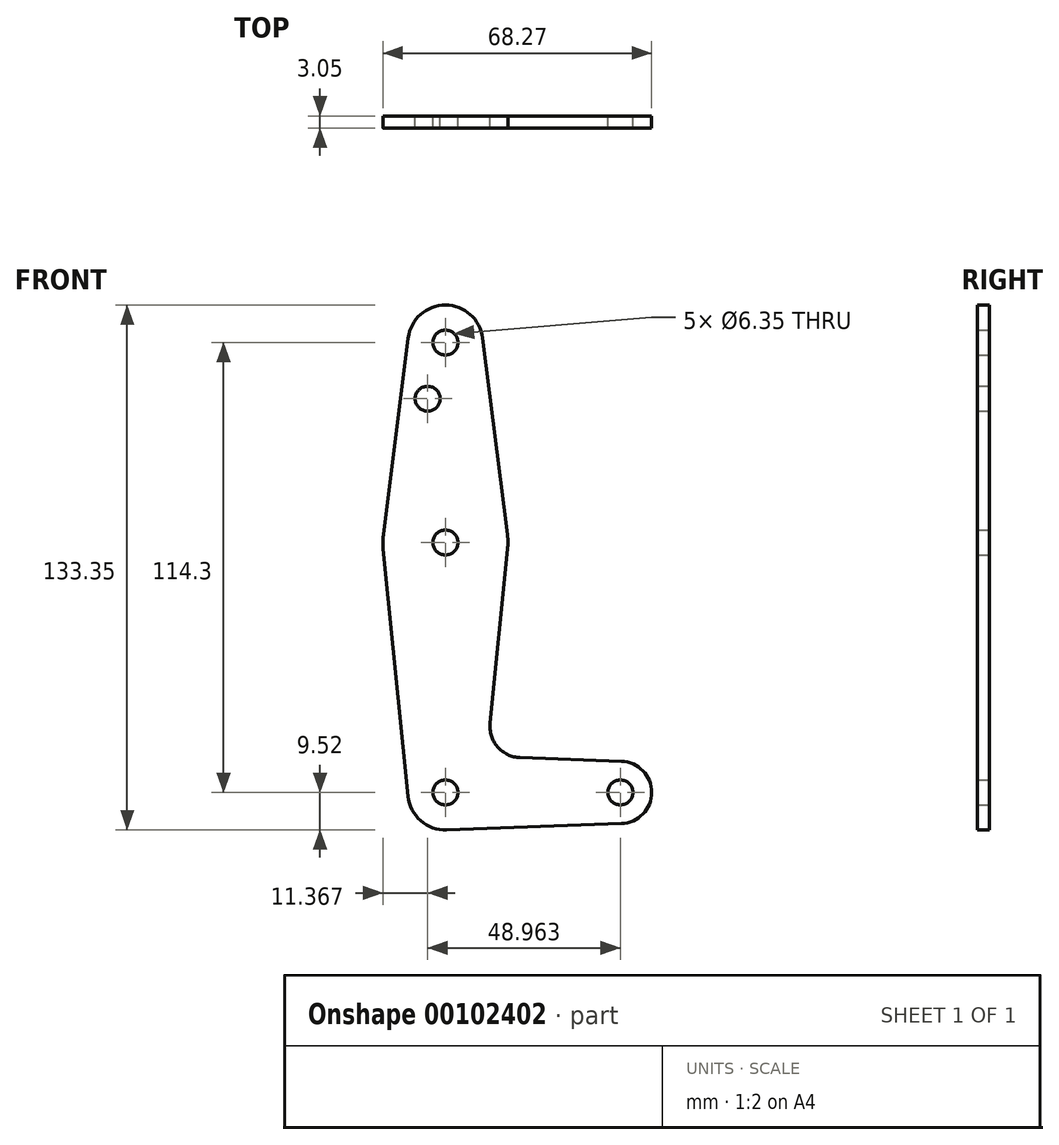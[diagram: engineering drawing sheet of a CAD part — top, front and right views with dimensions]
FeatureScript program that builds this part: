
annotation { "Feature Type Name" : "Feature", "Feature Type Description" : "" }
export const myFeature = defineFeature(function(context is Context, id is Id, definition is map)
    precondition{}
    {
        {
            var Q0;
            Q0=qCreatedBy(makeId("Front.planeOp"),FACE);
            var sketch = newSketch(context, id + "F0", { "sketchPlane" : qUnion([Q0])});
            skLineSegment(sketch, "E0", {"start": v(0, 114.3) * mm, "end": v(0, 0) * mm, "construction": true});
            skLineSegment(sketch, "E1", {"start": v(0, 0) * mm, "end": v(51.84, 0) * mm, "construction": true});
            skCircle(sketch, "E2", {"center": v(0, 114.3) * mm, "radius": 9.53 * mm});
            skCircle(sketch, "E3", {"center": v(0, 63.5) * mm, "radius": 15.88 * mm});
            skCircle(sketch, "E4", {"center": v(0, 0) * mm, "radius": 9.53 * mm});
            skCircle(sketch, "E5", {"center": v(44.45, 0) * mm, "radius": 7.94 * mm});
            skLineSegment(sketch, "E6", {"start": v(-9.45, 115.5) * mm, "end": v(-15.75, 65.48) * mm});
            skLineSegment(sketch, "E7", {"start": v(9.45, 115.5) * mm, "end": v(15.75, 65.48) * mm});
            skLineSegment(sketch, "E8", {"start": v(15.8, 61.91) * mm, "end": v(11.34, 17.6) * mm});
            skLineSegment(sketch, "E9", {"start": v(-15.8, 61.91) * mm, "end": v(-9.48, -0.95) * mm});
            skLineSegment(sketch, "E10", {"start": v(18.97, 8.85) * mm, "end": v(44.73, 7.93) * mm});
            skLineSegment(sketch, "E11", {"start": v(0.34, -9.52) * mm, "end": v(44.73, -7.93) * mm});
            skCircle(sketch, "E12", {"center": v(0, 114.3) * mm, "radius": 3.18 * mm});
            skCircle(sketch, "E13", {"center": v(-4.51, 100.03) * mm, "radius": 3.18 * mm});
            skCircle(sketch, "E14", {"center": v(0, 63.5) * mm, "radius": 3.18 * mm});
            skCircle(sketch, "E15", {"center": v(0, 0) * mm, "radius": 3.18 * mm});
            skCircle(sketch, "E16", {"center": v(44.45, 0) * mm, "radius": 3.18 * mm});
            skArc(sketch, "E17.filletArc", {"start": v(11.34, 17.6) * mm, "mid": v(13.26, 11.57) * mm, "end": v(18.97, 8.85) * mm});
            skSolve(sketch);
        }
        {
            var Q0;
            Q0 = qSketchRegion(id + "F0", true);
            extrude(context, id + "F1", {"entities" : qUnion([Q0]), "depth" : 3.05 * mm});
        }
    });
